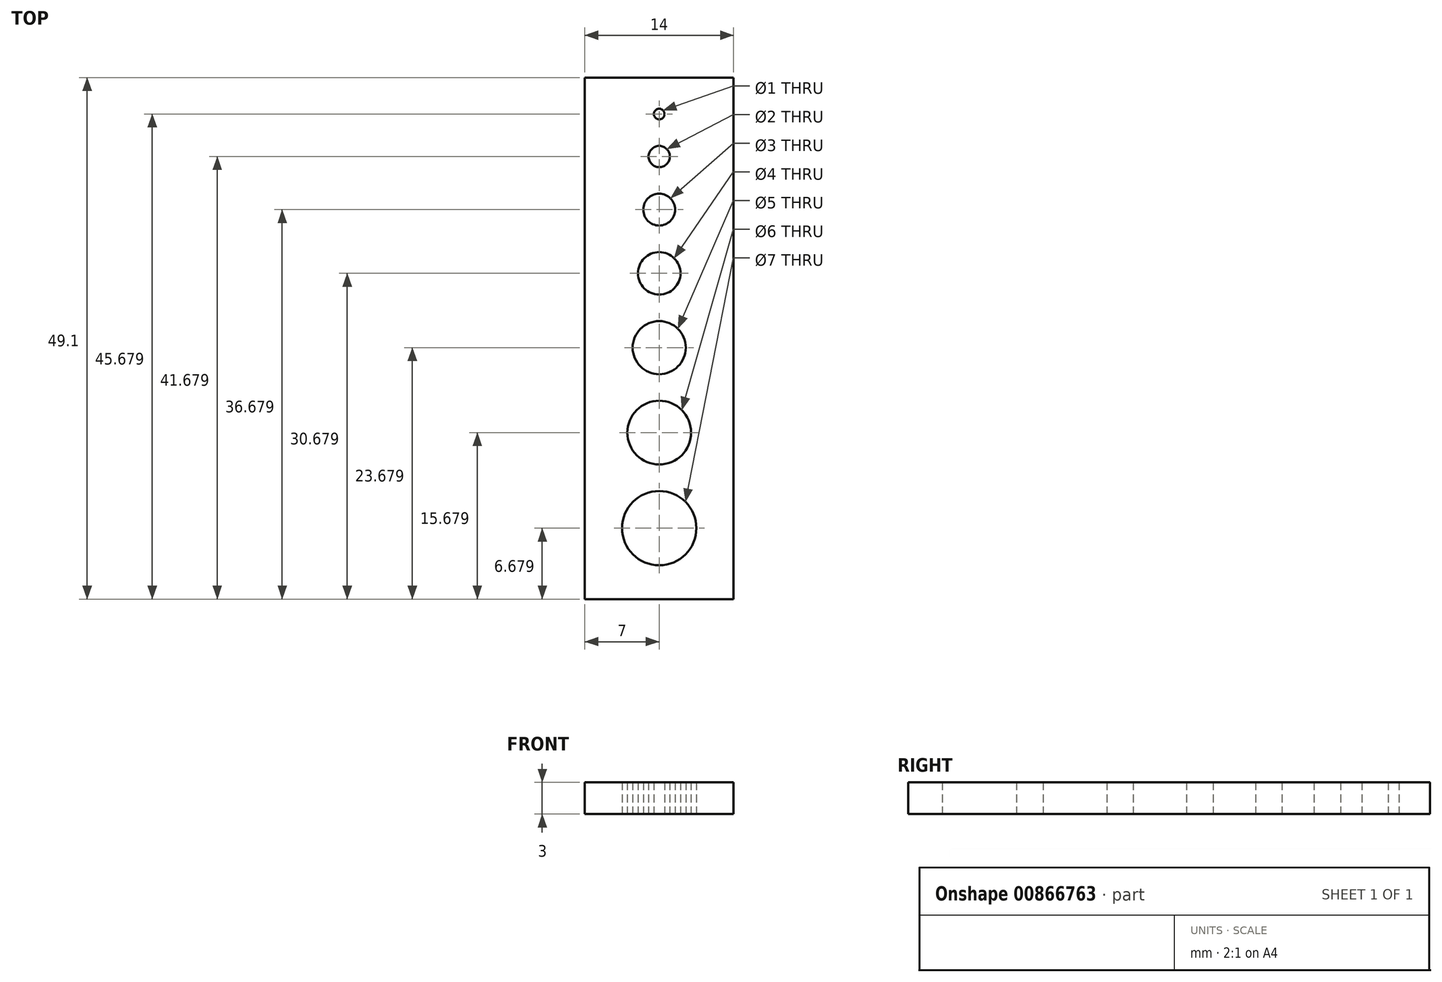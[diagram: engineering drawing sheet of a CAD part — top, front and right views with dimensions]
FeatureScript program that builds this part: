
annotation { "Feature Type Name" : "Feature", "Feature Type Description" : "" }
export const myFeature = defineFeature(function(context is Context, id is Id, definition is map)
    precondition{}
    {
        {
            var Q0;
            Q0=qCreatedBy(makeId("Top.planeOp"),FACE);
            var sketch = newSketch(context, id + "F0", { "sketchPlane" : qUnion([Q0])});
            skCircle(sketch, "E0", {"center": v(0, 12.3) * mm, "radius": 0.5 * mm});
            skCircle(sketch, "E1", {"center": v(0, 8.3) * mm, "radius": 1 * mm});
            skCircle(sketch, "E2", {"center": v(0, 3.3) * mm, "radius": 1.5 * mm});
            skCircle(sketch, "E3", {"center": v(0, -2.7) * mm, "radius": 2 * mm});
            skCircle(sketch, "E4", {"center": v(0, -9.7) * mm, "radius": 2.5 * mm});
            skCircle(sketch, "E5", {"center": v(0, -17.7) * mm, "radius": 3 * mm});
            skCircle(sketch, "E6", {"center": v(0, -26.7) * mm, "radius": 3.5 * mm});
            skLineSegment(sketch, "E7.bottom", {"start": v(-7, 15.73) * mm, "end": v(7, 15.73) * mm});
            skLineSegment(sketch, "E7.top", {"start": v(-7, -33.37) * mm, "end": v(7, -33.37) * mm});
            skLineSegment(sketch, "E7.left", {"start": v(-7, 15.73) * mm, "end": v(-7, -33.37) * mm});
            skLineSegment(sketch, "E7.right", {"start": v(7, 15.73) * mm, "end": v(7, -33.37) * mm});
            skSolve(sketch);
        }
        {
            var Q0;
            Q0=makeQuery(id+"F0.imprint","IMPRINT",FACE,{"disambiguationData":[TD([[makeQuery(id+"F0.imprint","IMPRINT",EDGE,{"derivedFrom":sQuery(id+"F0.wireOp",EDGE,"E0")}),-1.0]])]});
            extrude(context, id + "F1", {"entities" : qUnion([Q0]), "depth" : 3 * mm, "offsetDistance" : 25 * mm});
        }
    });
